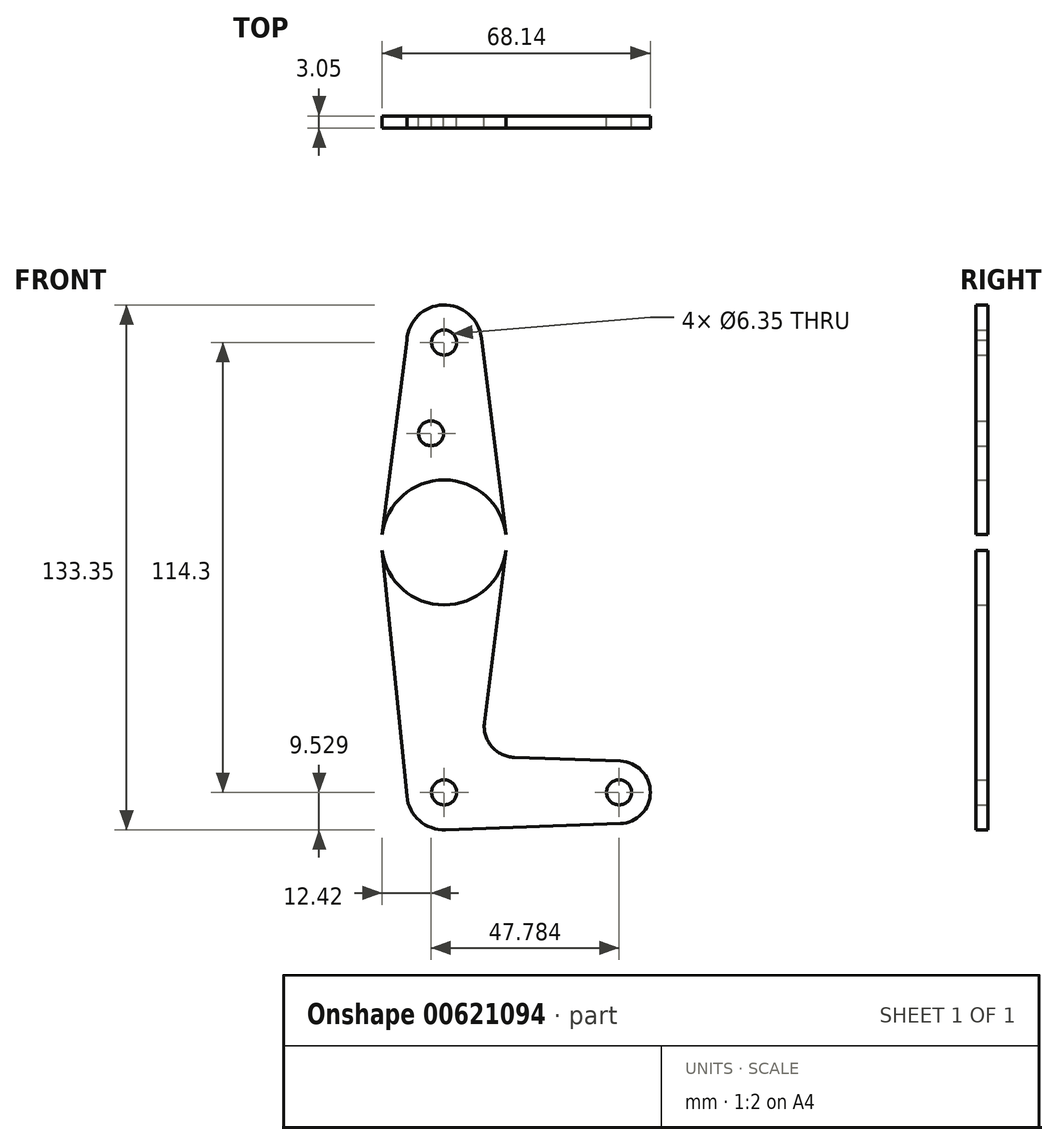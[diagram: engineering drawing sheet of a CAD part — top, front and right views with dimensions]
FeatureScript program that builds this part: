
annotation { "Feature Type Name" : "Feature", "Feature Type Description" : "" }
export const myFeature = defineFeature(function(context is Context, id is Id, definition is map)
    precondition{}
    {
        {
            var Q0;
            Q0=qCreatedBy(makeId("Front.planeOp"),FACE);
            var sketch = newSketch(context, id + "F0", { "sketchPlane" : qUnion([Q0])});
            skLineSegment(sketch, "E0", {"start": v(-34.4, 84.32) * mm, "end": v(-34.4, -29.98) * mm});
            skLineSegment(sketch, "E1", {"start": v(-34.4, -29.98) * mm, "end": v(10.04, -29.98) * mm});
            skCircle(sketch, "E2", {"center": v(-34.4, 84.32) * mm, "radius": 9.52 * mm});
            skCircle(sketch, "E3", {"center": v(-34.4, 33.52) * mm, "radius": 15.88 * mm});
            skCircle(sketch, "E4", {"center": v(-34.4, -29.98) * mm, "radius": 9.53 * mm});
            skCircle(sketch, "E5", {"center": v(10.04, -29.98) * mm, "radius": 7.94 * mm});
            skLineSegment(sketch, "E6", {"start": v(-43.9, 84.98) * mm, "end": v(-50.16, 35.5) * mm});
            skLineSegment(sketch, "E7", {"start": v(-50.16, 31.53) * mm, "end": v(-43.88, -30.93) * mm});
            skLineSegment(sketch, "E8", {"start": v(-24.17, -12.15) * mm, "end": v(-18.66, 31.53) * mm});
            skLineSegment(sketch, "E9", {"start": v(-18.66, 35.5) * mm, "end": v(-24.96, 85.5) * mm});
            skLineSegment(sketch, "E10", {"start": v(-16.57, -21.1) * mm, "end": v(10.33, -22.05) * mm});
            skLineSegment(sketch, "E11", {"start": v(10.33, -37.91) * mm, "end": v(-34.4, -39.51) * mm});
            skCircle(sketch, "E12", {"center": v(-34.4, 84.32) * mm, "radius": 3.18 * mm});
            skCircle(sketch, "E13", {"center": v(-34.4, 33.52) * mm, "radius": 3.18 * mm});
            skCircle(sketch, "E14", {"center": v(-34.4, -29.98) * mm, "radius": 3.18 * mm});
            skCircle(sketch, "E15", {"center": v(10.04, -29.98) * mm, "radius": 3.18 * mm});
            skCircle(sketch, "E16", {"center": v(-37.74, 61.25) * mm, "radius": 3.18 * mm});
            skPoint(sketch, "E17.newPointA", {"position": v(-34.4, -20.46) * mm});
            skArc(sketch, "E17.filletArc", {"start": v(-24.17, -12.15) * mm, "mid": v(-22.34, -18.3) * mm, "end": v(-16.57, -21.1) * mm});
            skSolve(sketch);
        }
        {
            var Q0;
            Q0=makeQuery(id+"F0.imprint","IMPRINT",FACE,{"disambiguationData":[TD([[makeQuery(id+"F0.imprint","IMPRINT",EDGE,{"derivedFrom":sQuery(id+"F0.wireOp",EDGE,"E12")}),-1.0]])]});
            var Q1;
            {var subQ5=sQuery(id+"F0.wireOp",EDGE,"E9");Q1=makeQuery(id+"F0.imprint","IMPRINT",FACE,{"disambiguationData":[TD([[makeQuery(id+"F0.imprint","IMPRINT",EDGE,{"derivedFrom":subQ5}),1.0]])]});}
            var Q2;
            {var subQ0=sQuery(id+"F0.wireOp",EDGE,"E6");Q2=makeQuery(id+"F0.imprint","IMPRINT",FACE,{"disambiguationData":[TD([[makeQuery(id+"F0.imprint","IMPRINT",EDGE,{"derivedFrom":subQ0}),1.0]])]});}
            var Q3;
            {var subQ0=sQuery(id+"F0.wireOp",EDGE,"E3");var subQ3=sQuery(id+"F0.wireOp",EDGE,"E0");var subQ4=makeQuery(id+"F0.imprint","INTERSECT",VERTEX,{"disambiguationData":[OD(0.0)],"derivedFrom":[subQ3,subQ0]});Q3=makeQuery(id+"F0.imprint","IMPRINT",FACE,{"disambiguationData":[TD([[makeQuery(id+"F0.imprint","IMPRINT",EDGE,{"disambiguationData":[TD([[subQ4,-1.0]])],"derivedFrom":subQ3}),-1.0]])]});}
            var Q4;
            {var subQ0=sQuery(id+"F0.wireOp",EDGE,"E3");var subQ2=sQuery(id+"F0.wireOp",EDGE,"E0");var subQ5=makeQuery(id+"F0.imprint","INTERSECT",VERTEX,{"disambiguationData":[OD(0.0)],"derivedFrom":[subQ2,subQ0]});Q4=makeQuery(id+"F0.imprint","IMPRINT",FACE,{"disambiguationData":[TD([[makeQuery(id+"F0.imprint","IMPRINT",EDGE,{"disambiguationData":[TD([[subQ5,-1.0]])],"derivedFrom":subQ2}),1.0]])]});}
            var Q5;
            {var subQ5=sQuery(id+"F0.wireOp",EDGE,"E7");Q5=makeQuery(id+"F0.imprint","IMPRINT",FACE,{"disambiguationData":[TD([[makeQuery(id+"F0.imprint","IMPRINT",EDGE,{"derivedFrom":subQ5}),1.0]])]});}
            var Q6;
            {var subQ0=sQuery(id+"F0.wireOp",EDGE,"E8");Q6=makeQuery(id+"F0.imprint","IMPRINT",FACE,{"disambiguationData":[TD([[makeQuery(id+"F0.imprint","IMPRINT",EDGE,{"derivedFrom":subQ0}),1.0]])]});}
            var Q7;
            {var subQ0=sQuery(id+"F0.wireOp",EDGE,"E4");var subQ7=sQuery(id+"F0.wireOp",EDGE,"E0");var subQ8=makeQuery(id+"F0.imprint","INTERSECT",VERTEX,{"derivedFrom":[subQ7,subQ0]});Q7=makeQuery(id+"F0.imprint","IMPRINT",FACE,{"disambiguationData":[TD([[makeQuery(id+"F0.imprint","IMPRINT",EDGE,{"disambiguationData":[TD([[subQ8,-1.0]])],"derivedFrom":subQ7}),-1.0]])]});}
            var Q8;
            {var subQ0=sQuery(id+"F0.wireOp",EDGE,"E4");var subQ1=sQuery(id+"F0.wireOp",EDGE,"E0");var subQ2=makeQuery(id+"F0.imprint","INTERSECT",VERTEX,{"derivedFrom":[subQ1,subQ0]});Q8=makeQuery(id+"F0.imprint","IMPRINT",FACE,{"disambiguationData":[TD([[makeQuery(id+"F0.imprint","IMPRINT",EDGE,{"disambiguationData":[TD([[subQ2,-1.0]])],"derivedFrom":subQ1}),1.0]])]});}
            var Q9;
            {var subQ0=sQuery(id+"F0.wireOp",EDGE,"E5");var subQ1=sQuery(id+"F0.wireOp",EDGE,"E1");var subQ2=makeQuery(id+"F0.imprint","INTERSECT",VERTEX,{"derivedFrom":[subQ1,subQ0]});Q9=makeQuery(id+"F0.imprint","IMPRINT",FACE,{"disambiguationData":[TD([[makeQuery(id+"F0.imprint","IMPRINT",EDGE,{"disambiguationData":[TD([[subQ2,1.0]])],"derivedFrom":subQ1}),-1.0]])]});}
            var Q10;
            Q10=makeQuery(id+"F0.imprint","IMPRINT",FACE,{"disambiguationData":[TD([[makeQuery(id+"F0.imprint","IMPRINT",EDGE,{"derivedFrom":sQuery(id+"F0.wireOp",EDGE,"E15")}),-1.0]])]});
            extrude(context, id + "F1", {"entities" : qUnion([Q0, Q1, Q2, Q3, Q4, Q5, Q6, Q7, Q8, Q9, Q10]), "depth" : 3.05 * mm, "offsetDistance" : 25.4 * mm});
        }
    });
